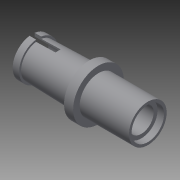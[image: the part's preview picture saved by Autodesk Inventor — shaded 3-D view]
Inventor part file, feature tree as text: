
AUTODESK INVENTOR PART (.ipt)
format: ipt  version: 2015 (Build 190159000, 159)  size: 147,968 bytes
history: native  units: in
note: dims shown in document units (in); Inventor stores cm internally (conversion verified against a paired STEP export)
features: sketch x2, revolve x1, extrude x1
ambient origin geometry x8: Origin, YZ Plane, XZ Plane, XY Plane, X Axis, Y Axis, Z Axis, Center Point
bodies: Solid1 (feature_tree)
feature tree (4):
  revolve  "Revolution1"  [1 undecoded]
  extrude  "Extrusion1"  Depth=0.04in
  sketch  "Sketch1"  dims[d0=0.33in d2=0.02in]
  sketch  "Sketch4"  dims[d3=0.03in d4=0.05in d5=0.07in d6=0.095in d7=0.01in d8=0.05in d9=0.05in d10=0.05in d11=0.19in d12=0.25in d13=0.025in d15=0.03in d16=90.0deg d18=0.04in d19=0.02in d21=0.0in d22=1.0in d23=0.2in d24=0.0in]
note: 1 required parameter value undecoded (feature->parameter linkage not recoverable at this tier; creation-order binding heuristic only, values carry confidence <= 0.55)
